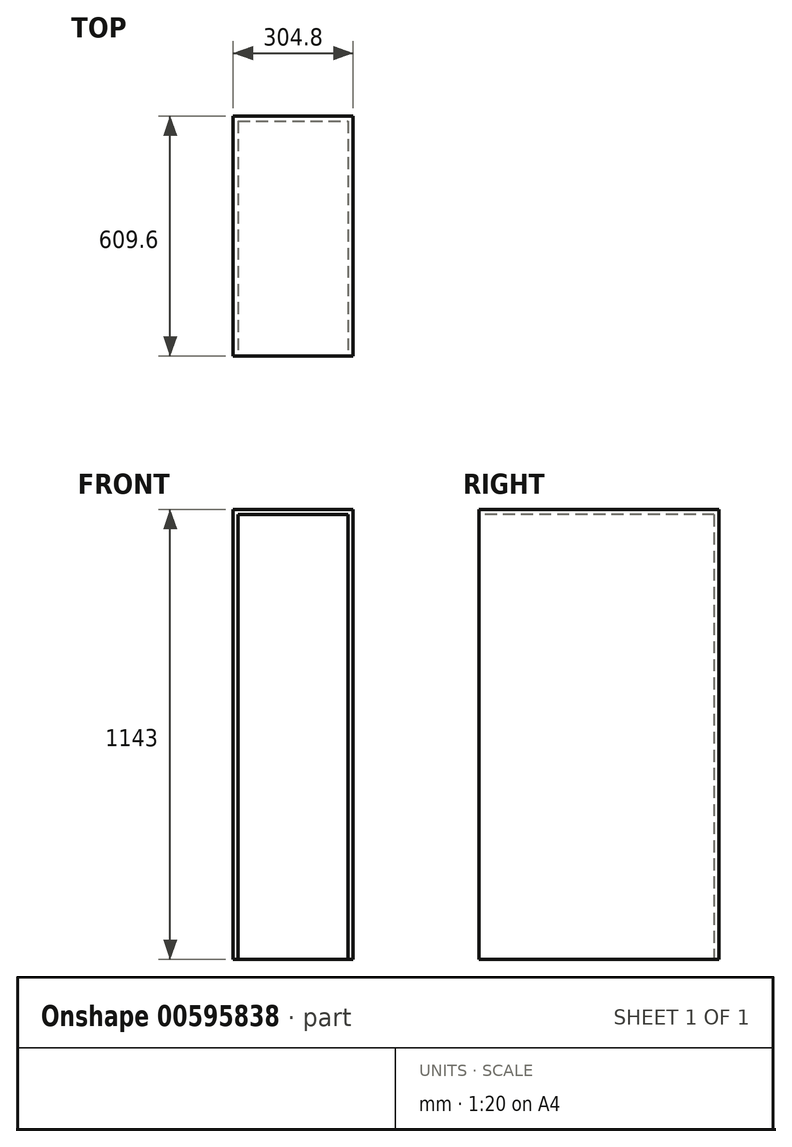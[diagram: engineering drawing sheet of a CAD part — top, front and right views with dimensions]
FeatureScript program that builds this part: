
annotation { "Feature Type Name" : "Feature", "Feature Type Description" : "" }
export const myFeature = defineFeature(function(context is Context, id is Id, definition is map)
    precondition{}
    {
        {
            var Q0;
            Q0=qCreatedBy(makeId("Top.planeOp"),FACE);
            var sketch = newSketch(context, id + "F0", { "sketchPlane" : qUnion([Q0])});
            skLineSegment(sketch, "E0.bottom", {"start": v(0, 0) * mm, "end": v(304.8, 0) * mm});
            skLineSegment(sketch, "E0.top", {"start": v(0, -609.6) * mm, "end": v(304.8, -609.6) * mm});
            skLineSegment(sketch, "E0.left", {"start": v(0, 0) * mm, "end": v(0, -609.6) * mm});
            skLineSegment(sketch, "E0.right", {"start": v(304.8, 0) * mm, "end": v(304.8, -609.6) * mm});
            skSolve(sketch);
        }
        {
            var Q0;
            Q0=qSketchRegion(id+"F0",true);
            extrude(context, id + "F1", {"entities" : qUnion([Q0]), "depth" : 1143 * mm, "offsetDistance" : 25.4 * mm});
        }
        {
            var Q0;
            Q0=makeQuery(id+"F1.opExtrude","SWEPT_FACE",FACE,{"disambiguationData":[OSD([sQuery(id+"F0.wireOp",EDGE,"E0.top")])]});
            shell(context, id + "F2", {"entities" : qUnion([Q0]), "thickness" : 12.7 * mm});
        }
        {
            var Q0;
            {var subQ0=sQuery(id+"F0.wireOp",EDGE,"E0.right");var subQ1=sQuery(id+"F0.wireOp",EDGE,"E0.left");var subQ2=sQuery(id+"F0.wireOp",EDGE,"E0.top");var subQ3=sQuery(id+"F0.wireOp",EDGE,"E0.bottom");Q0=makeQuery(id+"F2.opShell","OFFSET_FACE",FACE,{"disambiguationData":[OSD([subQ3,subQ2,subQ1,subQ0]),TDD([makeQuery(id+"F1.opExtrude","CAP_FACE",FACE,{"disambiguationData":[OSD([subQ3,subQ2,subQ1,subQ0])],"isStart":true})])]});}
            extrude(context, id + "F3", {"entities" : qUnion([Q0]), "operationType" : NewBodyOperationType.REMOVE, "endBound" : BoundingType.THROUGH_ALL, "oppositeDirection" : true, "depth" : 25.4 * mm, "offsetDistance" : 25.4 * mm});
        }
    });
